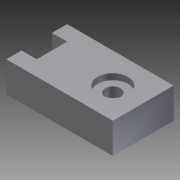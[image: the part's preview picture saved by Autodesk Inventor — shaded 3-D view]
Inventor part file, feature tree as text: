
AUTODESK INVENTOR PART (.ipt)
format: ipt  version: 2013 (Build 170138000, 138)  size: 99,328 bytes
history: native  units: mm
features: extrude x2, sketch x2
ambient origin geometry x8: Origin, YZ Plane, XZ Plane, XY Plane, X Axis, Y Axis, Z Axis, Center Point
bodies: Solid1 (feature_tree)
feature tree (4):
  extrude  "Extrusion1"  Depth=10.0mm
  extrude  "Extrusion2"  Depth=5.0mm
  sketch  "Sketch1"  dims[d0=5.0mm d1=10.0mm]
  sketch  "Sketch2"  dims[d2=5.0mm d3=5.0mm d4=5.0mm d5=35.0mm d7=10.0mm d8=5.0mm d9=10.0mm d10=0.0mm d11=10.0mm d12=2.0mm d13=0.0mm]
